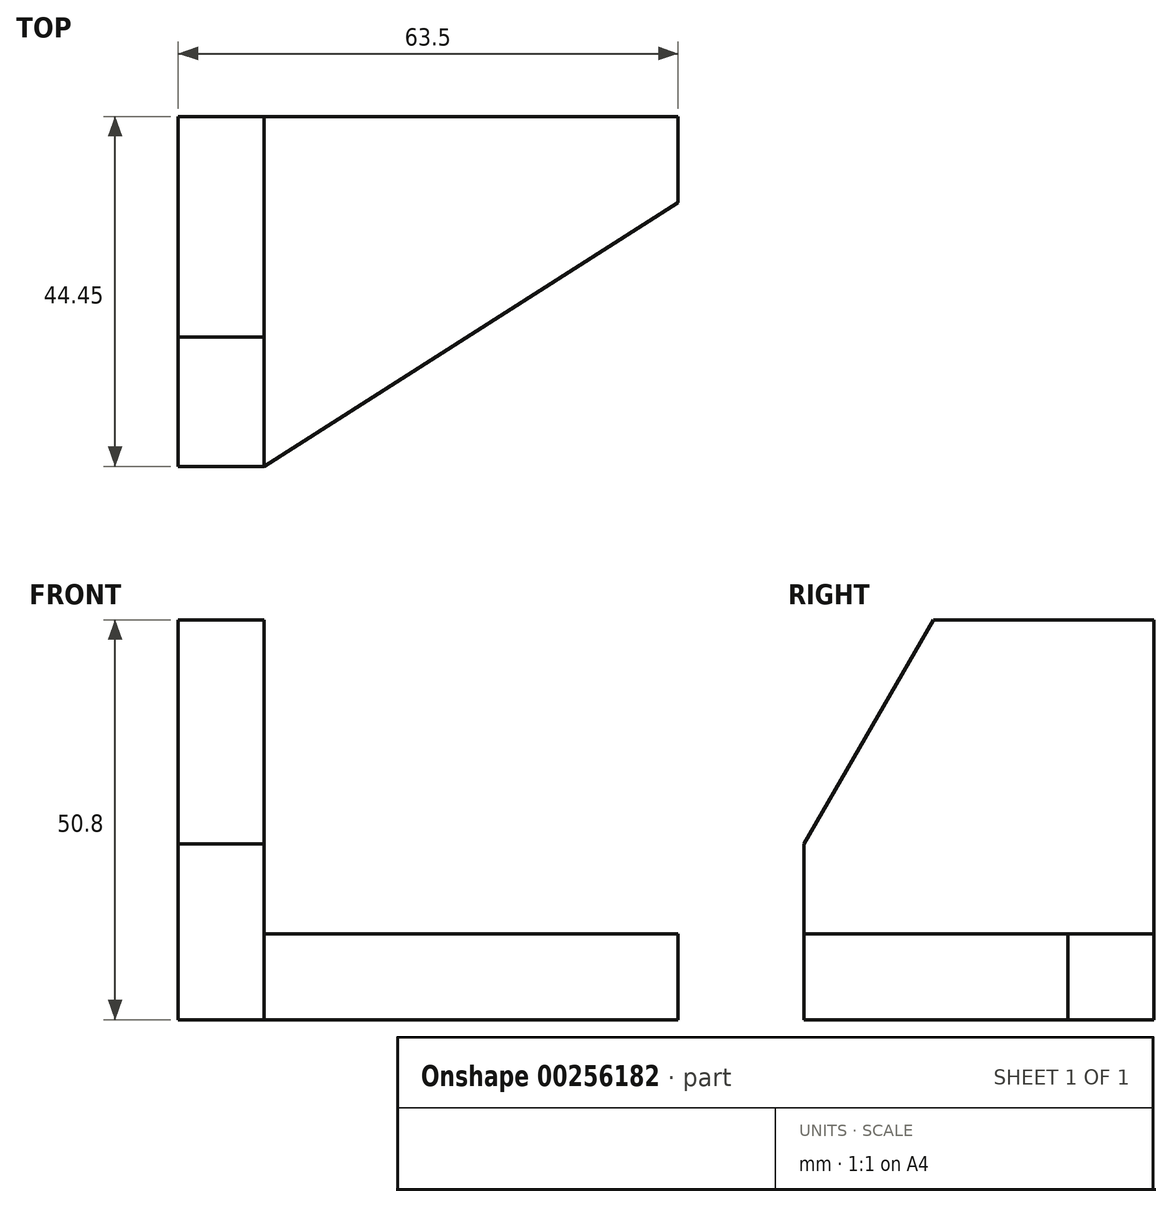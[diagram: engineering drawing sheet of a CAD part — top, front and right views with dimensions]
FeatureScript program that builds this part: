
annotation { "Feature Type Name" : "Feature", "Feature Type Description" : "" }
export const myFeature = defineFeature(function(context is Context, id is Id, definition is map)
    precondition{}
    {
        {
            var Q0;
            Q0=qCreatedBy(makeId("Front.planeOp"),FACE);
            var sketch = newSketch(context, id + "F0", { "sketchPlane" : qUnion([Q0])});
            skLineSegment(sketch, "E0", {"start": v(0, -60.2) * mm, "end": v(0, 0) * mm});
            skLineSegment(sketch, "E1", {"start": v(0, 0) * mm, "end": v(31.75, 0) * mm});
            skLineSegment(sketch, "E2", {"start": v(31.75, 0) * mm, "end": v(114.3, -22.12) * mm});
            skLineSegment(sketch, "E3", {"start": v(114.3, -22.12) * mm, "end": v(114.3, -60.2) * mm});
            skLineSegment(sketch, "E4", {"start": v(114.3, -60.2) * mm, "end": v(0, -60.2) * mm});
            skLineSegment(sketch, "E5", {"start": v(63.5, -49.28) * mm, "end": v(63.5, -60.2) * mm});
            skLineSegment(sketch, "E6", {"start": v(0, -60.2) * mm, "end": v(0, -9.4) * mm});
            skLineSegment(sketch, "E7", {"start": v(0, -9.4) * mm, "end": v(10.92, -9.4) * mm});
            skLineSegment(sketch, "E8", {"start": v(10.92, -9.4) * mm, "end": v(10.92, -49.28) * mm});
            skLineSegment(sketch, "E9", {"start": v(10.92, -49.28) * mm, "end": v(63.5, -49.28) * mm});
            skLineSegment(sketch, "E10.bottom", {"start": v(114.3, -60.2) * mm, "end": v(95.25, -60.2) * mm});
            skLineSegment(sketch, "E10.top", {"start": v(114.3, -41.15) * mm, "end": v(95.25, -41.15) * mm});
            skLineSegment(sketch, "E10.left", {"start": v(114.3, -60.2) * mm, "end": v(114.3, -41.15) * mm});
            skLineSegment(sketch, "E10.right", {"start": v(95.25, -60.2) * mm, "end": v(95.25, -41.15) * mm});
            skCircle(sketch, "E11", {"center": v(95.25, -41.15) * mm, "radius": 7.87 * mm});
            skSolve(sketch);
        }
        {
            var Q0;
            {var subQ1=sQuery(id+"F0.wireOp",EDGE,"E5");Q0=makeQuery(id+"F0.imprint","IMPRINT",FACE,{"disambiguationData":[TD([[makeQuery(id+"F0.imprint","IMPRINT",EDGE,{"derivedFrom":subQ1}),-1.0]])]});}
            extrude(context, id + "F1", {"entities" : qUnion([Q0]), "depth" : 44.45 * mm});
        }
        {
            var Q0;
            Q0=makeQuery(id+"F0.imprint","IMPRINT",FACE,{"disambiguationData":[TD([[makeQuery(id+"F0.imprint","IMPRINT",EDGE,{"derivedFrom":sQuery(id+"F0.wireOp",EDGE,"E0")}),-1.0]])]});
            var Q1;
            {var subQ1=sQuery(id+"F0.wireOp",EDGE,"E10.bottom");Q1=makeQuery(id+"F0.imprint","IMPRINT",FACE,{"disambiguationData":[TD([[makeQuery(id+"F0.imprint","IMPRINT",EDGE,{"derivedFrom":subQ1}),-1.0]])]});}
            extrude(context, id + "F2", {"entities" : qUnion([Q0, Q1]), "operationType" : NewBodyOperationType.ADD, "depth" : 10.92 * mm});
        }
        {
            var Q0;
            Q0=makeQuery(id+"F1.opExtrude","SWEPT_FACE",FACE,{"disambiguationData":[OSD([sQuery(id+"F0.wireOp",EDGE,"E9")])]});
            var sketch = newSketch(context, id + "F3", { "sketchPlane" : qUnion([Q0])});
            skLineSegment(sketch, "E12", {"start": v(10.92, -44.45) * mm, "end": v(63.5, -10.92) * mm});
            skSolve(sketch);
        }
        {
            var Q0;
            Q0=makeQuery(id+"F3.imprint","IMPRINT",FACE,{"disambiguationData":[TD([[makeQuery(id+"F3.imprint","IMPRINT",EDGE,{"derivedFrom":sQuery(id+"F3.wireOp",EDGE,"E12")}),-1.0]])]});
            extrude(context, id + "F4", {"entities" : qUnion([Q0]), "operationType" : NewBodyOperationType.REMOVE, "oppositeDirection" : true, "depth" : 10.92 * mm});
        }
        {
            var Q0;
            Q0=makeQuery(id+"F1.opExtrude","SWEPT_FACE",FACE,{"disambiguationData":[OSD([sQuery(id+"F0.wireOp",EDGE,"E8")])]});
            var sketch = newSketch(context, id + "F5", { "sketchPlane" : qUnion([Q0])});
            skPoint(sketch, "E13", {"position": v(-44.57, -38.1) * mm});
            skLineSegment(sketch, "E14.bottom", {"start": v(-44.57, -38.1) * mm, "end": v(-28, -38.1) * mm});
            skLineSegment(sketch, "E14.top", {"start": v(-44.57, -9.4) * mm, "end": v(-28, -9.4) * mm});
            skLineSegment(sketch, "E14.left", {"start": v(-44.57, -38.1) * mm, "end": v(-44.57, -9.4) * mm});
            skLineSegment(sketch, "E14.right", {"start": v(-28, -38.1) * mm, "end": v(-28, -9.4) * mm});
            skLineSegment(sketch, "E15", {"start": v(-44.57, -38.1) * mm, "end": v(-28, -9.4) * mm});
            skSolve(sketch);
        }
        {
            var Q0;
            {var subQ0=sQuery(id+"F5.wireOp",EDGE,"E14.top");var subQ1=sQuery(id+"F0.wireOp",EDGE,"E8");var subQ2=makeQuery(id+"F1.opExtrude","CAP_EDGE",EDGE,{"disambiguationData":[OSD([subQ1])],"isStart":false});var subQ3=makeQuery(id+"F5.imprint","INTERSECT",VERTEX,{"derivedFrom":[subQ2,subQ0]});Q0=makeQuery(id+"F5.imprint","IMPRINT",FACE,{"disambiguationData":[TD([[makeQuery(id+"F5.imprint","IMPRINT",EDGE,{"disambiguationData":[TD([[subQ3,-1.0]])],"derivedFrom":subQ2}),1.0]])]});}
            extrude(context, id + "F6", {"entities" : qUnion([Q0]), "operationType" : NewBodyOperationType.REMOVE, "oppositeDirection" : true, "depth" : 10.92 * mm});
        }
    });
